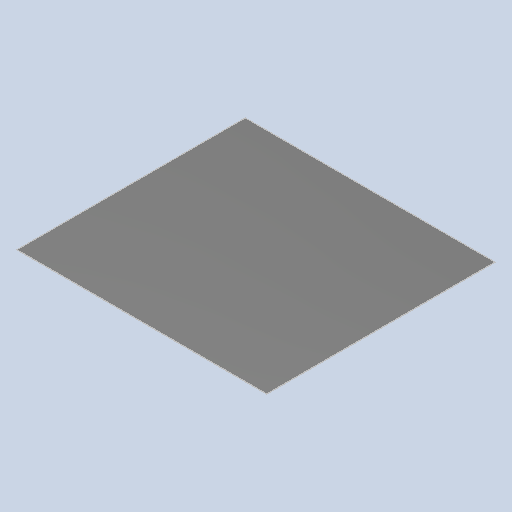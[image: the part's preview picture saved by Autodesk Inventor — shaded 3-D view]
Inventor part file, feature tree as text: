
AUTODESK INVENTOR PART (.ipt)
format: ipt  version: 2023 (Build 270158000, 158)  size: 96,256 bytes
history: native  units: in
note: dims shown in document units (in); Inventor stores cm internally (conversion verified against a paired STEP export)
features: extrude x1, sketch x1
ambient origin geometry x8: Origin, YZ Plane, XZ Plane, XY Plane, X Axis, Y Axis, Z Axis, Center Point
bodies: Solid1 (feature_tree)
feature tree (2):
  extrude  "Extrusion1"  Depth=1.8346in
  sketch  "Sketch1"  dims[d0=1.6772in d1=1.8346in d2=0.0031in d3=0.0in]
